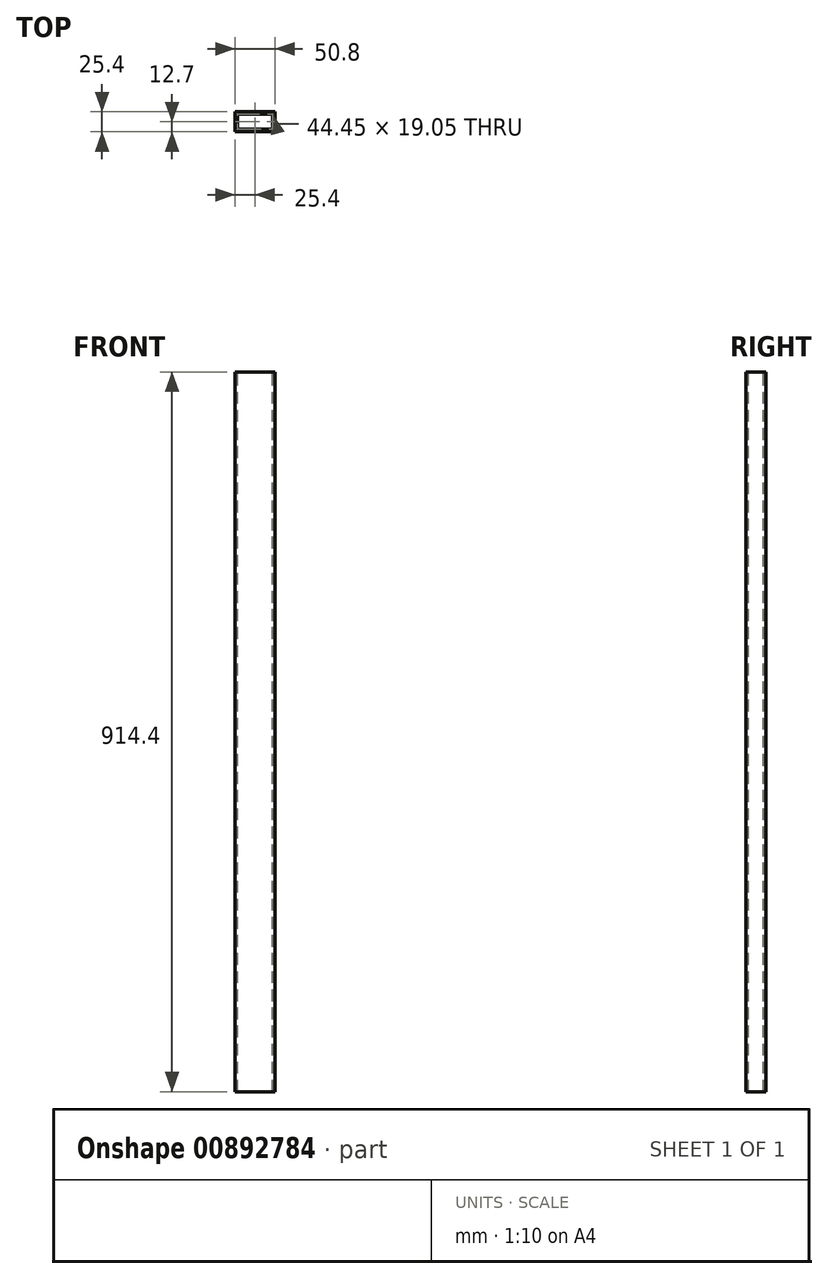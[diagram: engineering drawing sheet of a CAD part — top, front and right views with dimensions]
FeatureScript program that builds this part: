
annotation { "Feature Type Name" : "Feature", "Feature Type Description" : "" }
export const myFeature = defineFeature(function(context is Context, id is Id, definition is map)
    precondition{}
    {
        {
            var Q0;
            Q0=qCreatedBy(makeId("Top.planeOp"),FACE);
            var sketch = newSketch(context, id + "F0", { "sketchPlane" : qUnion([Q0])});
            skPoint(sketch, "E0.0", {"position": v(0, 0) * mm});
            skLineSegment(sketch, "E1.bottom", {"start": v(25.4, 12.7) * mm, "end": v(-25.4, 12.7) * mm});
            skLineSegment(sketch, "E1.top", {"start": v(25.4, -12.7) * mm, "end": v(-25.4, -12.7) * mm});
            skLineSegment(sketch, "E1.left", {"start": v(25.4, 12.7) * mm, "end": v(25.4, -12.7) * mm});
            skLineSegment(sketch, "E1.right", {"start": v(-25.4, 12.7) * mm, "end": v(-25.4, -12.7) * mm});
            skSolve(sketch);
        }
        {
            var Q0;
            Q0=makeQuery(id+"F0.imprint","IMPRINT",FACE,{"disambiguationData":[TD([[makeQuery(id+"F0.imprint","IMPRINT",EDGE,{"derivedFrom":sQuery(id+"F0.wireOp",EDGE,"E1.bottom")}),1.0]])]});
            extrude(context, id + "F1", {"entities" : qUnion([Q0]), "endBound" : BoundingType.SYMMETRIC, "depth" : 914.4 * mm, "offsetDistance" : 25.4 * mm});
        }
        {
            var Q0;
            Q0=makeQuery(id+"F1.opExtrude","CAP_FACE",FACE,{"disambiguationData":[OSD([sQuery(id+"F0.wireOp",EDGE,"E1.bottom"),sQuery(id+"F0.wireOp",EDGE,"E1.top"),sQuery(id+"F0.wireOp",EDGE,"E1.left"),sQuery(id+"F0.wireOp",EDGE,"E1.right")])],"isStart":false});
            var sketch = newSketch(context, id + "F2", { "sketchPlane" : qUnion([Q0])});
            skLineSegment(sketch, "E2.bottom", {"start": v(22.23, 9.53) * mm, "end": v(-22.23, 9.53) * mm});
            skLineSegment(sketch, "E2.top", {"start": v(22.23, -9.53) * mm, "end": v(-22.23, -9.53) * mm});
            skLineSegment(sketch, "E2.left", {"start": v(22.23, 9.53) * mm, "end": v(22.23, -9.53) * mm});
            skLineSegment(sketch, "E2.right", {"start": v(-22.23, 9.53) * mm, "end": v(-22.23, -9.53) * mm});
            skPoint(sketch, "E2.middle", {"position": v(0, 0) * mm});
            skSolve(sketch);
        }
        {
            var Q0;
            Q0 = qSketchRegion(id + "F2", true);
            extrude(context, id + "F3", {"entities" : qUnion([Q0]), "operationType" : NewBodyOperationType.REMOVE, "endBound" : BoundingType.SYMMETRIC, "oppositeDirection" : true, "depth" : 914.4 * mm, "offsetDistance" : 25.4 * mm});
        }
        {
            var Q0;
            Q0=makeQuery(id+"F3.boolean.opBoolean","COPY",FACE,{"derivedFrom":makeQuery(id+"F3.opExtrude","CAP_FACE",FACE,{"disambiguationData":[OSD([sQuery(id+"F2.wireOp",EDGE,"E2.bottom"),sQuery(id+"F2.wireOp",EDGE,"E2.top"),sQuery(id+"F2.wireOp",EDGE,"E2.left"),sQuery(id+"F2.wireOp",EDGE,"E2.right")])],"isStart":false})});
            extrude(context, id + "F4", {"entities" : qUnion([Q0]), "operationType" : NewBodyOperationType.REMOVE, "oppositeDirection" : true, "depth" : 914.4 * mm, "offsetDistance" : 25.4 * mm});
        }
    });
